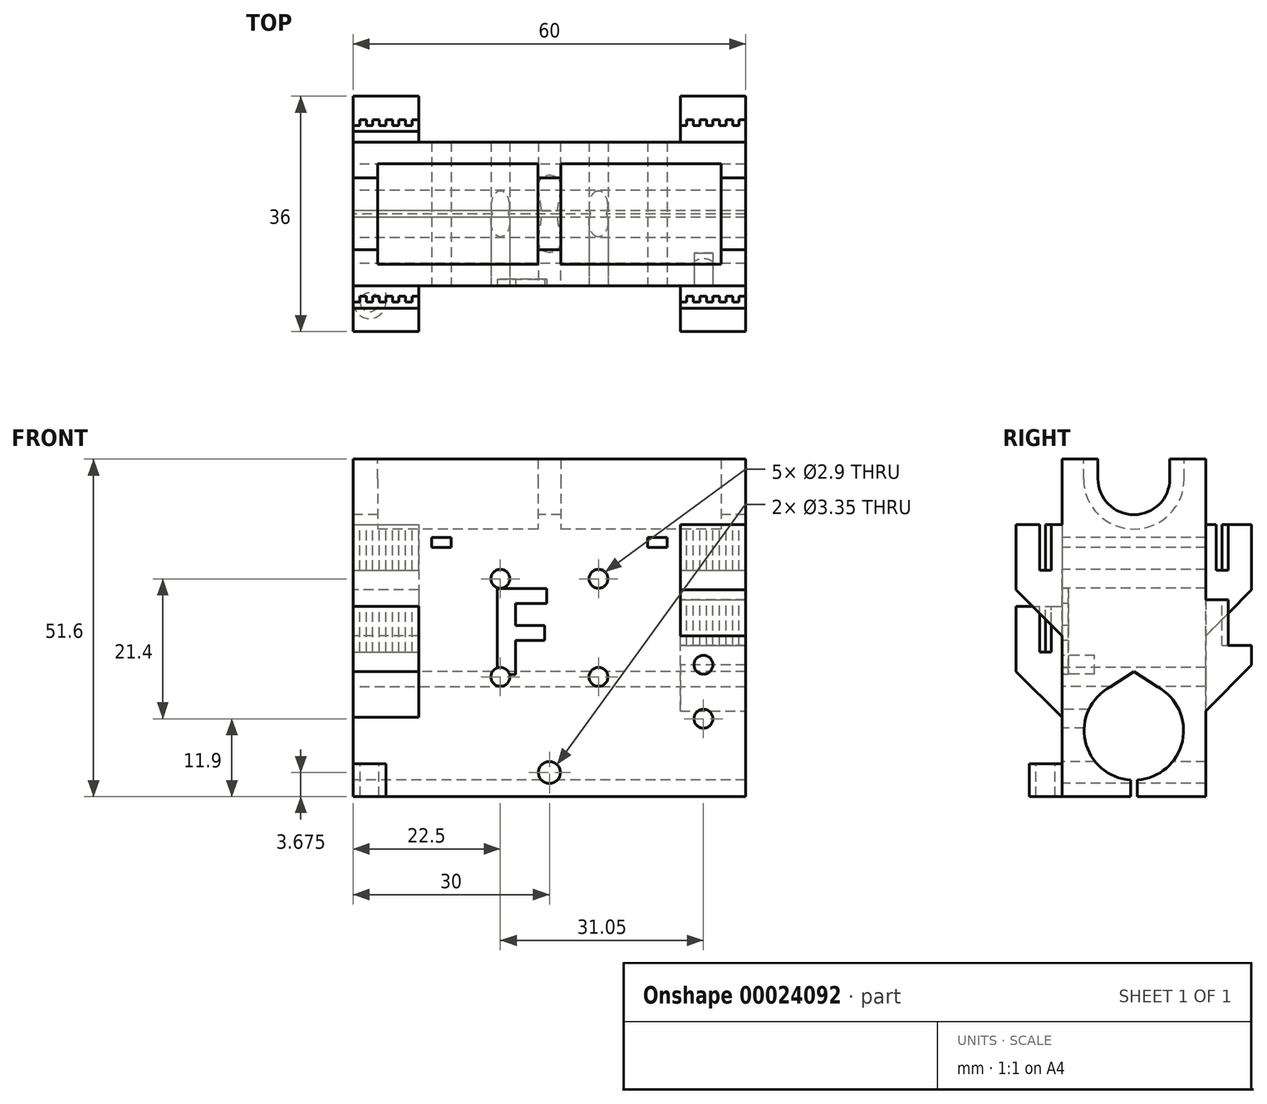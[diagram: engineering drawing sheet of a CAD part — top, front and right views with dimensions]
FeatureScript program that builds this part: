
annotation { "Feature Type Name" : "Feature", "Feature Type Description" : "" }
export const myFeature = defineFeature(function(context is Context, id is Id, definition is map)
    precondition{}
    {
        {
            var Q0;
            Q0=qCreatedBy(makeId("Top.planeOp"),FACE);
            var sketch = newSketch(context, id + "F0", { "sketchPlane" : qUnion([Q0])});
            skLineSegment(sketch, "E0.bottom", {"start": v(0, 0) * mm, "end": v(60, 0) * mm});
            skLineSegment(sketch, "E0.top", {"start": v(0, 22) * mm, "end": v(60, 22) * mm});
            skLineSegment(sketch, "E0.left", {"start": v(0, 0) * mm, "end": v(0, 22) * mm});
            skLineSegment(sketch, "E0.right", {"start": v(60, 0) * mm, "end": v(60, 22) * mm});
            skSolve(sketch);
        }
        {
            var Q0;
            Q0=qSketchRegion(id+"F0",true);
            extrude(context, id + "F1", {"entities" : qUnion([Q0]), "depth" : 51.6 * mm});
        }
        {
            var Q0;
            Q0=makeQuery(id+"F1.opExtrude","SWEPT_FACE",FACE,{"disambiguationData":[OSD([sQuery(id+"F0.wireOp",EDGE,"E0.left")])]});
            var sketch = newSketch(context, id + "F2", { "sketchPlane" : qUnion([Q0])});
            skCircle(sketch, "E1", {"center": v(-11, 10.1) * mm, "radius": 7.6 * mm});
            skCircle(sketch, "E2", {"center": v(-11, 48.6) * mm, "radius": 5.5 * mm});
            skLineSegment(sketch, "E3", {"start": v(-22, 48.6) * mm, "end": v(0, 48.6) * mm, "construction": true});
            skLineSegment(sketch, "E4", {"start": v(-16.5, 51.6) * mm, "end": v(-16.5, 48.6) * mm});
            skLineSegment(sketch, "E5", {"start": v(-5.5, 51.6) * mm, "end": v(-5.5, 48.6) * mm});
            skLineSegment(sketch, "E6", {"start": v(-22, 10.1) * mm, "end": v(0, 10.1) * mm, "construction": true});
            skLineSegment(sketch, "E7", {"start": v(-11, 10.1) * mm, "end": v(-11, 0) * mm, "construction": true});
            skLineSegment(sketch, "E8", {"start": v(-11, 0) * mm, "end": v(-11.5, 0) * mm});
            skLineSegment(sketch, "E9", {"start": v(-11.5, 0) * mm, "end": v(-11.5, 2.52) * mm});
            skLineSegment(sketch, "E10", {"start": v(-11.5, 2.52) * mm, "end": v(-10.5, 2.52) * mm});
            skLineSegment(sketch, "E11", {"start": v(-10.5, 2.52) * mm, "end": v(-10.5, 0) * mm});
            skLineSegment(sketch, "E12", {"start": v(-10.5, 0) * mm, "end": v(-11, 0) * mm});
            skLineSegment(sketch, "E13", {"start": v(-11, 17.7) * mm, "end": v(-11, 19.08) * mm});
            skLineSegment(sketch, "E14", {"start": v(-11, 19.08) * mm, "end": v(-6.5, 16.22) * mm});
            skLineSegment(sketch, "E15", {"start": v(-11, 19.08) * mm, "end": v(-15.5, 16.22) * mm});
            skCircle(sketch, "E16", {"center": v(-11, 48.6) * mm, "radius": 7.7 * mm});
            skLineSegment(sketch, "E17", {"start": v(-3.3, 48.6) * mm, "end": v(-3.3, 51.6) * mm});
            skLineSegment(sketch, "E18", {"start": v(-18.7, 48.6) * mm, "end": v(-18.7, 51.6) * mm});
            skSolve(sketch);
        }
        {
            var Q0;
            {var subQ0=sQuery(id+"F2.wireOp",EDGE,"E14");var subQ1=sQuery(id+"F2.wireOp",EDGE,"E1");var subQ3=makeQuery(id+"F2.imprint","INTERSECT",VERTEX,{"disambiguationData":[OD(0.0)],"derivedFrom":[subQ1,subQ0]});Q0=makeQuery(id+"F2.imprint","IMPRINT",FACE,{"disambiguationData":[TD([[makeQuery(id+"F2.imprint","IMPRINT",EDGE,{"disambiguationData":[TD([[subQ3,-1.0]])],"derivedFrom":subQ1}),1.0]])]});}
            var Q1;
            {var subQ0=sQuery(id+"F2.wireOp",EDGE,"E15");var subQ1=sQuery(id+"F2.wireOp",EDGE,"E1");var subQ3=makeQuery(id+"F2.imprint","INTERSECT",VERTEX,{"disambiguationData":[OD(0.0)],"derivedFrom":[subQ1,subQ0]});Q1=makeQuery(id+"F2.imprint","IMPRINT",FACE,{"disambiguationData":[TD([[makeQuery(id+"F2.imprint","IMPRINT",EDGE,{"disambiguationData":[TD([[subQ3,1.0]])],"derivedFrom":subQ1}),1.0]])]});}
            var Q2;
            Q2=makeQuery(id+"F2.imprint","IMPRINT",FACE,{"disambiguationData":[TD([[makeQuery(id+"F2.imprint","IMPRINT",EDGE,{"derivedFrom":sQuery(id+"F2.wireOp",EDGE,"E8")}),-1.0]])]});
            var Q3;
            {var subQ0=sQuery(id+"F2.wireOp",EDGE,"E10");Q3=makeQuery(id+"F2.imprint","IMPRINT",FACE,{"disambiguationData":[TD([[makeQuery(id+"F2.imprint","IMPRINT",EDGE,{"derivedFrom":subQ0}),-1.0]])]});}
            var Q4;
            {var subQ3=sQuery(id+"F2.wireOp",EDGE,"E13");Q4=makeQuery(id+"F2.imprint","IMPRINT",FACE,{"disambiguationData":[TD([[makeQuery(id+"F2.imprint","IMPRINT",EDGE,{"derivedFrom":subQ3}),-1.0]])]});}
            var Q5;
            {var subQ3=sQuery(id+"F2.wireOp",EDGE,"E13");Q5=makeQuery(id+"F2.imprint","IMPRINT",FACE,{"disambiguationData":[TD([[makeQuery(id+"F2.imprint","IMPRINT",EDGE,{"derivedFrom":subQ3}),1.0]])]});}
            var Q6;
            {var subQ7=sQuery(id+"F2.wireOp",EDGE,"E10");Q6=makeQuery(id+"F2.imprint","IMPRINT",FACE,{"disambiguationData":[TD([[makeQuery(id+"F2.imprint","IMPRINT",EDGE,{"derivedFrom":subQ7}),1.0]])]});}
            var Q7;
            {var subQ3=sQuery(id+"F2.wireOp",EDGE,"E5");Q7=makeQuery(id+"F2.imprint","IMPRINT",FACE,{"disambiguationData":[TD([[makeQuery(id+"F2.imprint","IMPRINT",EDGE,{"derivedFrom":subQ3}),-1.0]])]});}
            var Q8;
            {var subQ0=sQuery(id+"F2.wireOp",EDGE,"E4");Q8=makeQuery(id+"F2.imprint","IMPRINT",FACE,{"disambiguationData":[TD([[makeQuery(id+"F2.imprint","IMPRINT",EDGE,{"derivedFrom":subQ0}),1.0]])]});}
            var Q9;
            {var subQ0=sQuery(id+"F2.wireOp",EDGE,"E4");Q9=makeQuery(id+"F2.imprint","IMPRINT",FACE,{"disambiguationData":[TD([[makeQuery(id+"F2.imprint","IMPRINT",EDGE,{"derivedFrom":subQ0}),1.0]])]});}
            var Q10;
            {var subQ3=sQuery(id+"F2.wireOp",EDGE,"E5");Q10=makeQuery(id+"F2.imprint","IMPRINT",FACE,{"disambiguationData":[TD([[makeQuery(id+"F2.imprint","IMPRINT",EDGE,{"derivedFrom":subQ3}),-1.0]])]});}
            var Q11;
            {var subQ1=sQuery(id+"F2.wireOp",EDGE,"E2");var subQ4=makeQuery(id+"F2.imprint","INTERSECT",VERTEX,{"derivedFrom":[subQ1,sQuery(id+"F2.wireOp",EDGE,"E5")]});Q11=makeQuery(id+"F2.imprint","IMPRINT",FACE,{"disambiguationData":[TD([[makeQuery(id+"F2.imprint","IMPRINT",EDGE,{"disambiguationData":[TD([[subQ4,-1.0]])],"derivedFrom":subQ1}),1.0]])]});}
            extrude(context, id + "F3", {"entities" : qUnion([Q0, Q1, Q2, Q3, Q4, Q5, Q6, Q7, Q8, Q9, Q10, Q11]), "operationType" : NewBodyOperationType.REMOVE, "endBound" : BoundingType.THROUGH_ALL, "oppositeDirection" : true, "depth" : 25 * mm});
        }
        {
            var Q0;
            {var subQ3=sQuery(id+"F2.wireOp",EDGE,"E4");Q0=makeQuery(id+"F2.imprint","IMPRINT",FACE,{"disambiguationData":[TD([[makeQuery(id+"F2.imprint","IMPRINT",EDGE,{"derivedFrom":subQ3}),-1.0]])]});}
            var Q1;
            {var subQ3=sQuery(id+"F2.wireOp",EDGE,"E18");Q1=makeQuery(id+"F2.imprint","IMPRINT",FACE,{"disambiguationData":[TD([[makeQuery(id+"F2.imprint","IMPRINT",EDGE,{"derivedFrom":subQ3}),-1.0]])]});}
            var Q2;
            {var subQ3=sQuery(id+"F2.wireOp",EDGE,"E17");Q2=makeQuery(id+"F2.imprint","IMPRINT",FACE,{"disambiguationData":[TD([[makeQuery(id+"F2.imprint","IMPRINT",EDGE,{"derivedFrom":subQ3}),1.0]])]});}
            extrude(context, id + "F4", {"entities" : qUnion([Q0, Q1, Q2]), "operationType" : NewBodyOperationType.REMOVE, "oppositeDirection" : true, "depth" : 56.25 * mm});
        }
        {
            var Q0;
            {var subQ3=sQuery(id+"F2.wireOp",EDGE,"E4");Q0=makeQuery(id+"F2.imprint","IMPRINT",FACE,{"disambiguationData":[TD([[makeQuery(id+"F2.imprint","IMPRINT",EDGE,{"derivedFrom":subQ3}),-1.0]])]});}
            var Q1;
            {var subQ3=sQuery(id+"F2.wireOp",EDGE,"E18");Q1=makeQuery(id+"F2.imprint","IMPRINT",FACE,{"disambiguationData":[TD([[makeQuery(id+"F2.imprint","IMPRINT",EDGE,{"derivedFrom":subQ3}),-1.0]])]});}
            var Q2;
            {var subQ3=sQuery(id+"F2.wireOp",EDGE,"E17");Q2=makeQuery(id+"F2.imprint","IMPRINT",FACE,{"disambiguationData":[TD([[makeQuery(id+"F2.imprint","IMPRINT",EDGE,{"derivedFrom":subQ3}),1.0]])]});}
            extrude(context, id + "F5", {"entities" : qUnion([Q0, Q1, Q2]), "operationType" : NewBodyOperationType.ADD, "oppositeDirection" : true, "depth" : 31.75 * mm});
        }
        {
            var Q0;
            {var subQ3=sQuery(id+"F2.wireOp",EDGE,"E4");Q0=makeQuery(id+"F2.imprint","IMPRINT",FACE,{"disambiguationData":[TD([[makeQuery(id+"F2.imprint","IMPRINT",EDGE,{"derivedFrom":subQ3}),-1.0]])]});}
            var Q1;
            {var subQ3=sQuery(id+"F2.wireOp",EDGE,"E18");Q1=makeQuery(id+"F2.imprint","IMPRINT",FACE,{"disambiguationData":[TD([[makeQuery(id+"F2.imprint","IMPRINT",EDGE,{"derivedFrom":subQ3}),-1.0]])]});}
            var Q2;
            {var subQ3=sQuery(id+"F2.wireOp",EDGE,"E17");Q2=makeQuery(id+"F2.imprint","IMPRINT",FACE,{"disambiguationData":[TD([[makeQuery(id+"F2.imprint","IMPRINT",EDGE,{"derivedFrom":subQ3}),1.0]])]});}
            extrude(context, id + "F6", {"entities" : qUnion([Q0, Q1, Q2]), "operationType" : NewBodyOperationType.REMOVE, "oppositeDirection" : true, "depth" : 28.25 * mm});
        }
        {
            var Q0;
            {var subQ3=sQuery(id+"F2.wireOp",EDGE,"E4");Q0=makeQuery(id+"F2.imprint","IMPRINT",FACE,{"disambiguationData":[TD([[makeQuery(id+"F2.imprint","IMPRINT",EDGE,{"derivedFrom":subQ3}),-1.0]])]});}
            var Q1;
            {var subQ3=sQuery(id+"F2.wireOp",EDGE,"E18");Q1=makeQuery(id+"F2.imprint","IMPRINT",FACE,{"disambiguationData":[TD([[makeQuery(id+"F2.imprint","IMPRINT",EDGE,{"derivedFrom":subQ3}),-1.0]])]});}
            var Q2;
            {var subQ3=sQuery(id+"F2.wireOp",EDGE,"E17");Q2=makeQuery(id+"F2.imprint","IMPRINT",FACE,{"disambiguationData":[TD([[makeQuery(id+"F2.imprint","IMPRINT",EDGE,{"derivedFrom":subQ3}),1.0]])]});}
            extrude(context, id + "F7", {"entities" : qUnion([Q0, Q1, Q2]), "operationType" : NewBodyOperationType.ADD, "oppositeDirection" : true, "depth" : 3.75 * mm});
        }
        {
            var Q0;
            Q0=makeQuery(id+"F1.opExtrude","SWEPT_FACE",FACE,{"disambiguationData":[OSD([sQuery(id+"F0.wireOp",EDGE,"E0.bottom")])]});
            var sketch = newSketch(context, id + "F8", { "sketchPlane" : qUnion([Q0])});
            skLineSegment(sketch, "E19.bottom", {"start": v(0, 29.1) * mm, "end": v(10, 29.1) * mm});
            skLineSegment(sketch, "E19.top", {"start": v(0, 9.1) * mm, "end": v(10, 9.1) * mm});
            skLineSegment(sketch, "E19.left", {"start": v(0, 29.1) * mm, "end": v(0, 9.1) * mm});
            skLineSegment(sketch, "E19.right", {"start": v(10, 29.1) * mm, "end": v(10, 9.1) * mm});
            skLineSegment(sketch, "E20.bottom", {"start": v(60, 41.6) * mm, "end": v(50, 41.6) * mm});
            skLineSegment(sketch, "E20.top", {"start": v(60, 21.6) * mm, "end": v(50, 21.6) * mm});
            skLineSegment(sketch, "E20.left", {"start": v(60, 41.6) * mm, "end": v(60, 21.6) * mm});
            skLineSegment(sketch, "E20.right", {"start": v(50, 41.6) * mm, "end": v(50, 21.6) * mm});
            skPoint(sketch, "E21", {"position": v(0, 48.6) * mm});
            skPoint(sketch, "E22", {"position": v(0, 8.6) * mm});
            skSolve(sketch);
        }
        {
            var Q0;
            Q0=qSketchRegion(id+"F8",true);
            extrude(context, id + "F9", {"entities" : qUnion([Q0]), "operationType" : NewBodyOperationType.ADD, "depth" : 7 * mm});
        }
        {
            var Q0;
            Q0=makeQuery(id+"F9.opExtrude","CAP_EDGE",EDGE,{"disambiguationData":[OSD([sQuery(id+"F8.wireOp",EDGE,"E19.top")])],"isStart":false});
            var Q1;
            Q1=makeQuery(id+"F9.opExtrude","CAP_EDGE",EDGE,{"disambiguationData":[OSD([sQuery(id+"F8.wireOp",EDGE,"E20.top")])],"isStart":false});
            chamfer(context, id + "F10", {"entities" : qUnion([Q0, Q1]), "width" : 10 * mm, "tangentPropagation" : true});
        }
        {
            var Q0;
            Q0=makeQuery(id+"F9.opExtrude","SWEPT_FACE",FACE,{"disambiguationData":[OSD([sQuery(id+"F8.wireOp",EDGE,"E19.bottom")])]});
            var sketch = newSketch(context, id + "F11", { "sketchPlane" : qUnion([Q0])});
            skLineSegment(sketch, "E23", {"start": v(-935.9, 0) * mm, "end": v(-935.88, -4.54) * mm});
            skLineSegment(sketch, "E24.left", {"start": v(0, -3.4) * mm, "end": v(0, -1.6) * mm});
            skLineSegment(sketch, "E25", {"start": v(6, -2.5) * mm, "end": v(7, -2.5) * mm});
            skLineSegment(sketch, "E26", {"start": v(4, -2.5) * mm, "end": v(5, -2.5) * mm});
            skLineSegment(sketch, "E27", {"start": v(0, -2.5) * mm, "end": v(1, -2.5) * mm});
            skLineSegment(sketch, "E28", {"start": v(7, -1.6) * mm, "end": v(8, -1.6) * mm});
            skLineSegment(sketch, "E29", {"start": v(2, -2.5) * mm, "end": v(3, -2.5) * mm});
            skLineSegment(sketch, "E30", {"start": v(3, -1.6) * mm, "end": v(4, -1.6) * mm});
            skLineSegment(sketch, "E31", {"start": v(8, -2.5) * mm, "end": v(9, -2.5) * mm});
            skLineSegment(sketch, "E32", {"start": v(8, -1.6) * mm, "end": v(8, -2.5) * mm});
            skLineSegment(sketch, "E33", {"start": v(9, -2.5) * mm, "end": v(9, -1.6) * mm});
            skLineSegment(sketch, "E34", {"start": v(10, -1.6) * mm, "end": v(10, -2.5) * mm});
            skLineSegment(sketch, "E35", {"start": v(6, -1.6) * mm, "end": v(6, -2.5) * mm});
            skLineSegment(sketch, "E36", {"start": v(2, -1.6) * mm, "end": v(2, -2.5) * mm});
            skLineSegment(sketch, "E37", {"start": v(1, -1.6) * mm, "end": v(2, -1.6) * mm});
            skLineSegment(sketch, "E38", {"start": v(1, -2.5) * mm, "end": v(1, -1.6) * mm});
            skLineSegment(sketch, "E39", {"start": v(9, -1.6) * mm, "end": v(10, -1.6) * mm});
            skLineSegment(sketch, "E40", {"start": v(5, -1.6) * mm, "end": v(6, -1.6) * mm});
            skLineSegment(sketch, "E41", {"start": v(5, -2.5) * mm, "end": v(5, -1.6) * mm});
            skLineSegment(sketch, "E42", {"start": v(3, -2.5) * mm, "end": v(3, -1.6) * mm});
            skLineSegment(sketch, "E43", {"start": v(4, -1.6) * mm, "end": v(4, -2.5) * mm});
            skLineSegment(sketch, "E44", {"start": v(7, -2.5) * mm, "end": v(7, -1.6) * mm});
            skLineSegment(sketch, "E45", {"start": v(0, -1.6) * mm, "end": v(0, -2.5) * mm});
            skLineSegment(sketch, "E46", {"start": v(10, -2.5) * mm, "end": v(10, -3.4) * mm});
            skLineSegment(sketch, "E47", {"start": v(0, -3.4) * mm, "end": v(10, -3.4) * mm});
            skLineSegment(sketch, "E48", {"start": v(5.3, -1.6) * mm, "end": v(5.3, 0) * mm});
            skSolve(sketch);
        }
        {
            var Q0;
            Q0=qSketchRegion(id+"F11",true);
            extrude(context, id + "F12", {"entities" : qUnion([Q0]), "operationType" : NewBodyOperationType.REMOVE, "oppositeDirection" : true, "depth" : 7 * mm});
        }
        {
            var Q0;
            Q0=makeQuery(id+"F9.opExtrude","SWEPT_FACE",FACE,{"disambiguationData":[OSD([sQuery(id+"F8.wireOp",EDGE,"E20.bottom")])]});
            var sketch = newSketch(context, id + "F13", { "sketchPlane" : qUnion([Q0])});
            skLineSegment(sketch, "E49.left", {"start": v(50, -3.4) * mm, "end": v(50, -1.6) * mm});
            skLineSegment(sketch, "E50", {"start": v(56, -2.5) * mm, "end": v(57, -2.5) * mm});
            skLineSegment(sketch, "E51", {"start": v(54, -2.5) * mm, "end": v(55, -2.5) * mm});
            skLineSegment(sketch, "E52", {"start": v(50, -2.5) * mm, "end": v(51, -2.5) * mm});
            skLineSegment(sketch, "E53", {"start": v(57, -1.6) * mm, "end": v(58, -1.6) * mm});
            skLineSegment(sketch, "E54", {"start": v(52, -2.5) * mm, "end": v(53, -2.5) * mm});
            skLineSegment(sketch, "E55", {"start": v(53, -1.6) * mm, "end": v(54, -1.6) * mm});
            skLineSegment(sketch, "E56", {"start": v(58, -2.5) * mm, "end": v(59, -2.5) * mm});
            skLineSegment(sketch, "E57", {"start": v(58, -1.6) * mm, "end": v(58, -2.5) * mm});
            skLineSegment(sketch, "E58", {"start": v(59, -2.5) * mm, "end": v(59, -1.6) * mm});
            skLineSegment(sketch, "E59", {"start": v(60, -1.6) * mm, "end": v(60, -2.5) * mm});
            skLineSegment(sketch, "E60", {"start": v(56, -1.6) * mm, "end": v(56, -2.5) * mm});
            skLineSegment(sketch, "E61", {"start": v(52, -1.6) * mm, "end": v(52, -2.5) * mm});
            skLineSegment(sketch, "E62", {"start": v(51, -1.6) * mm, "end": v(52, -1.6) * mm});
            skLineSegment(sketch, "E63", {"start": v(51, -2.5) * mm, "end": v(51, -1.6) * mm});
            skLineSegment(sketch, "E64", {"start": v(59, -1.6) * mm, "end": v(60, -1.6) * mm});
            skLineSegment(sketch, "E65", {"start": v(55, -1.6) * mm, "end": v(56, -1.6) * mm});
            skLineSegment(sketch, "E66", {"start": v(55, -2.5) * mm, "end": v(55, -1.6) * mm});
            skLineSegment(sketch, "E67", {"start": v(53, -2.5) * mm, "end": v(53, -1.6) * mm});
            skLineSegment(sketch, "E68", {"start": v(54, -1.6) * mm, "end": v(54, -2.5) * mm});
            skLineSegment(sketch, "E69", {"start": v(57, -2.5) * mm, "end": v(57, -1.6) * mm});
            skLineSegment(sketch, "E70", {"start": v(50, -1.6) * mm, "end": v(50, -2.5) * mm});
            skLineSegment(sketch, "E71", {"start": v(60, -2.5) * mm, "end": v(60, -3.4) * mm});
            skLineSegment(sketch, "E72", {"start": v(50, -3.4) * mm, "end": v(60, -3.4) * mm});
            skLineSegment(sketch, "E73", {"start": v(55.23, -1.6) * mm, "end": v(55.23, 0) * mm});
            skSolve(sketch);
        }
        {
            var Q0;
            Q0=qSketchRegion(id+"F13",true);
            extrude(context, id + "F14", {"entities" : qUnion([Q0]), "operationType" : NewBodyOperationType.REMOVE, "oppositeDirection" : true, "depth" : 7 * mm});
        }
        {
            var Q0;
            Q0=makeQuery(id+"F1.opExtrude","SWEPT_FACE",FACE,{"disambiguationData":[OSD([sQuery(id+"F0.wireOp",EDGE,"E0.top")])]});
            var sketch = newSketch(context, id + "F15", { "sketchPlane" : qUnion([Q0])});
            skLineSegment(sketch, "E74.bottom", {"start": v(-60, 10.1) * mm, "end": v(-50, 10.1) * mm});
            skLineSegment(sketch, "E74.top", {"start": v(-60, 30.1) * mm, "end": v(-50, 30.1) * mm});
            skLineSegment(sketch, "E74.left", {"start": v(-60, 10.1) * mm, "end": v(-60, 30.1) * mm});
            skLineSegment(sketch, "E74.right", {"start": v(-50, 10.1) * mm, "end": v(-50, 30.1) * mm});
            skLineSegment(sketch, "E75.bottom", {"start": v(0, 41.6) * mm, "end": v(-10, 41.6) * mm});
            skLineSegment(sketch, "E75.top", {"start": v(0, 21.6) * mm, "end": v(-10, 21.6) * mm});
            skLineSegment(sketch, "E75.left", {"start": v(0, 41.6) * mm, "end": v(0, 21.6) * mm});
            skLineSegment(sketch, "E75.right", {"start": v(-10, 41.6) * mm, "end": v(-10, 21.6) * mm});
            skSolve(sketch);
        }
        {
            var Q0;
            Q0=qSketchRegion(id+"F15",true);
            extrude(context, id + "F16", {"entities" : qUnion([Q0]), "operationType" : NewBodyOperationType.ADD, "depth" : 7 * mm});
        }
        {
            var Q0;
            Q0=makeQuery(id+"F16.opExtrude","SWEPT_FACE",FACE,{"disambiguationData":[OSD([sQuery(id+"F15.wireOp",EDGE,"E74.top")])]});
            var sketch = newSketch(context, id + "F17", { "sketchPlane" : qUnion([Q0])});
            skLineSegment(sketch, "E76.left", {"start": v(50, 23.6) * mm, "end": v(50, 25.4) * mm});
            skLineSegment(sketch, "E77", {"start": v(56, 24.5) * mm, "end": v(57, 24.5) * mm});
            skLineSegment(sketch, "E78", {"start": v(54, 24.5) * mm, "end": v(55, 24.5) * mm});
            skLineSegment(sketch, "E79", {"start": v(50, 24.5) * mm, "end": v(51, 24.5) * mm});
            skLineSegment(sketch, "E80", {"start": v(57, 25.4) * mm, "end": v(58, 25.4) * mm});
            skLineSegment(sketch, "E81", {"start": v(52, 24.5) * mm, "end": v(53, 24.5) * mm});
            skLineSegment(sketch, "E82", {"start": v(53, 25.4) * mm, "end": v(54, 25.4) * mm});
            skLineSegment(sketch, "E83", {"start": v(58, 24.5) * mm, "end": v(59, 24.5) * mm});
            skLineSegment(sketch, "E84", {"start": v(58, 25.4) * mm, "end": v(58, 24.5) * mm});
            skLineSegment(sketch, "E85", {"start": v(59, 24.5) * mm, "end": v(59, 25.4) * mm});
            skLineSegment(sketch, "E86", {"start": v(60, 25.4) * mm, "end": v(60, 24.5) * mm});
            skLineSegment(sketch, "E87", {"start": v(56, 25.4) * mm, "end": v(56, 24.5) * mm});
            skLineSegment(sketch, "E88", {"start": v(52, 25.4) * mm, "end": v(52, 24.5) * mm});
            skLineSegment(sketch, "E89", {"start": v(51, 25.4) * mm, "end": v(52, 25.4) * mm});
            skLineSegment(sketch, "E90", {"start": v(51, 24.5) * mm, "end": v(51, 25.4) * mm});
            skLineSegment(sketch, "E91", {"start": v(59, 25.4) * mm, "end": v(60, 25.4) * mm});
            skLineSegment(sketch, "E92", {"start": v(55, 25.4) * mm, "end": v(56, 25.4) * mm});
            skLineSegment(sketch, "E93", {"start": v(55, 24.5) * mm, "end": v(55, 25.4) * mm});
            skLineSegment(sketch, "E94", {"start": v(53, 24.5) * mm, "end": v(53, 25.4) * mm});
            skLineSegment(sketch, "E95", {"start": v(54, 25.4) * mm, "end": v(54, 24.5) * mm});
            skLineSegment(sketch, "E96", {"start": v(57, 24.5) * mm, "end": v(57, 25.4) * mm});
            skLineSegment(sketch, "E97", {"start": v(50, 25.4) * mm, "end": v(50, 24.5) * mm});
            skLineSegment(sketch, "E98", {"start": v(60, 24.5) * mm, "end": v(60, 23.6) * mm});
            skLineSegment(sketch, "E99", {"start": v(50, 23.6) * mm, "end": v(60, 23.6) * mm});
            skLineSegment(sketch, "E100", {"start": v(55, 23.6) * mm, "end": v(55, 22) * mm});
            skSolve(sketch);
        }
        {
            var Q0;
            {var subQ4=sQuery(id+"F17.wireOp",EDGE,"E76.left");Q0=makeQuery(id+"F17.imprint","IMPRINT",FACE,{"disambiguationData":[TD([[makeQuery(id+"F17.imprint","IMPRINT",EDGE,{"derivedFrom":subQ4}),1.0]])]});}
            extrude(context, id + "F18", {"entities" : qUnion([Q0]), "operationType" : NewBodyOperationType.REMOVE, "oppositeDirection" : true, "depth" : 7 * mm});
        }
        {
            var Q0;
            Q0=makeQuery(id+"F16.opExtrude","SWEPT_FACE",FACE,{"disambiguationData":[OSD([sQuery(id+"F15.wireOp",EDGE,"E75.bottom")])]});
            var sketch = newSketch(context, id + "F19", { "sketchPlane" : qUnion([Q0])});
            skLineSegment(sketch, "E101", {"start": v(6, 24.5) * mm, "end": v(7, 24.5) * mm});
            skLineSegment(sketch, "E102", {"start": v(4, 24.5) * mm, "end": v(5, 24.5) * mm});
            skLineSegment(sketch, "E103", {"start": v(0, 24.5) * mm, "end": v(1, 24.5) * mm});
            skLineSegment(sketch, "E104", {"start": v(7, 25.4) * mm, "end": v(8, 25.4) * mm});
            skLineSegment(sketch, "E105", {"start": v(2, 24.5) * mm, "end": v(3, 24.5) * mm});
            skLineSegment(sketch, "E106", {"start": v(3, 25.4) * mm, "end": v(4, 25.4) * mm});
            skLineSegment(sketch, "E107", {"start": v(8, 24.5) * mm, "end": v(9, 24.5) * mm});
            skLineSegment(sketch, "E108", {"start": v(8, 25.4) * mm, "end": v(8, 24.5) * mm});
            skLineSegment(sketch, "E109", {"start": v(9, 24.5) * mm, "end": v(9, 25.4) * mm});
            skLineSegment(sketch, "E110", {"start": v(10, 25.4) * mm, "end": v(10, 24.5) * mm});
            skLineSegment(sketch, "E111", {"start": v(6, 25.4) * mm, "end": v(6, 24.5) * mm});
            skLineSegment(sketch, "E112", {"start": v(2, 25.4) * mm, "end": v(2, 24.5) * mm});
            skLineSegment(sketch, "E113", {"start": v(1, 25.4) * mm, "end": v(2, 25.4) * mm});
            skLineSegment(sketch, "E114", {"start": v(1, 24.5) * mm, "end": v(1, 25.4) * mm});
            skLineSegment(sketch, "E115", {"start": v(9, 25.4) * mm, "end": v(10, 25.4) * mm});
            skLineSegment(sketch, "E116", {"start": v(5, 25.4) * mm, "end": v(6, 25.4) * mm});
            skLineSegment(sketch, "E117", {"start": v(5, 24.5) * mm, "end": v(5, 25.4) * mm});
            skLineSegment(sketch, "E118", {"start": v(3, 24.5) * mm, "end": v(3, 25.4) * mm});
            skLineSegment(sketch, "E119", {"start": v(4, 25.4) * mm, "end": v(4, 24.5) * mm});
            skLineSegment(sketch, "E120", {"start": v(7, 24.5) * mm, "end": v(7, 25.4) * mm});
            skLineSegment(sketch, "E121", {"start": v(10, 24.5) * mm, "end": v(10, 23.6) * mm});
            skLineSegment(sketch, "E122", {"start": v(0, 23.6) * mm, "end": v(10, 23.6) * mm});
            skLineSegment(sketch, "E123", {"start": v(5, 23.6) * mm, "end": v(5, 22) * mm});
            skLineSegment(sketch, "E124", {"start": v(0, 23.6) * mm, "end": v(0, 24.5) * mm});
            skSolve(sketch);
        }
        {
            var Q0;
            Q0=makeQuery(id+"F19.imprint","IMPRINT",FACE,{"disambiguationData":[TD([[makeQuery(id+"F19.imprint","IMPRINT",EDGE,{"derivedFrom":sQuery(id+"F19.wireOp",EDGE,"E101")}),-1.0]])]});
            extrude(context, id + "F20", {"entities" : qUnion([Q0]), "operationType" : NewBodyOperationType.REMOVE, "oppositeDirection" : true, "depth" : 7 * mm});
        }
        {
            var Q0;
            Q0=makeQuery(id+"F16.opExtrude","CAP_EDGE",EDGE,{"disambiguationData":[OSD([sQuery(id+"F15.wireOp",EDGE,"E75.top")])],"isStart":false});
            var Q1;
            Q1=makeQuery(id+"F16.opExtrude","CAP_EDGE",EDGE,{"disambiguationData":[OSD([sQuery(id+"F15.wireOp",EDGE,"E74.bottom")])],"isStart":false});
            chamfer(context, id + "F21", {"entities" : qUnion([Q0, Q1]), "width" : 10 * mm, "tangentPropagation" : true});
        }
        {
            var Q0;
            Q0=makeQuery(id+"F1.opExtrude","SWEPT_FACE",FACE,{"disambiguationData":[OSD([sQuery(id+"F0.wireOp",EDGE,"E0.bottom")])]});
            var sketch = newSketch(context, id + "F22", { "sketchPlane" : qUnion([Q0])});
            skCircle(sketch, "E125", {"center": v(22.5, 33.3) * mm, "radius": 1.45 * mm});
            skCircle(sketch, "E126", {"center": v(37.5, 33.3) * mm, "radius": 1.45 * mm});
            skCircle(sketch, "E127", {"center": v(22.5, 18.3) * mm, "radius": 1.45 * mm});
            skCircle(sketch, "E128", {"center": v(37.5, 18.3) * mm, "radius": 1.45 * mm});
            skLineSegment(sketch, "E129", {"start": v(22.5, 33.3) * mm, "end": v(0, 33.3) * mm});
            skLineSegment(sketch, "E130", {"start": v(37.5, 18.3) * mm, "end": v(60, 18.3) * mm});
            skLineSegment(sketch, "E131", {"start": v(37.5, 33.3) * mm, "end": v(37.5, 51.6) * mm});
            skLineSegment(sketch, "E132", {"start": v(22.5, 18.3) * mm, "end": v(22.5, 0) * mm});
            skCircle(sketch, "E133", {"center": v(30, 3.68) * mm, "radius": 1.68 * mm});
            skLineSegment(sketch, "E134", {"start": v(30, 0) * mm, "end": v(30, 13.82) * mm, "construction": true});
            skSolve(sketch);
        }
        {
            var Q0;
            Q0=qSketchRegion(id+"F22",true);
            var Q1;
            Q1=makeQuery(id+"F22.imprint","IMPRINT",FACE,{"disambiguationData":[TD([[makeQuery(id+"F22.imprint","IMPRINT",EDGE,{"derivedFrom":sQuery(id+"F22.wireOp",EDGE,"E125")}),1.0]])]});
            var Q2;
            Q2=makeQuery(id+"F22.imprint","IMPRINT",FACE,{"disambiguationData":[TD([[makeQuery(id+"F22.imprint","IMPRINT",EDGE,{"derivedFrom":sQuery(id+"F22.wireOp",EDGE,"E126")}),1.0]])]});
            var Q3;
            Q3=makeQuery(id+"F22.imprint","IMPRINT",FACE,{"disambiguationData":[TD([[makeQuery(id+"F22.imprint","IMPRINT",EDGE,{"derivedFrom":sQuery(id+"F22.wireOp",EDGE,"E128")}),1.0]])]});
            var Q4;
            Q4=makeQuery(id+"F22.imprint","IMPRINT",FACE,{"disambiguationData":[TD([[makeQuery(id+"F22.imprint","IMPRINT",EDGE,{"derivedFrom":sQuery(id+"F22.wireOp",EDGE,"E127")}),1.0]])]});
            extrude(context, id + "F23", {"entities" : qUnion([Q0, Q1, Q2, Q3, Q4]), "operationType" : NewBodyOperationType.REMOVE, "endBound" : BoundingType.THROUGH_ALL, "oppositeDirection" : true, "depth" : 25 * mm});
        }
        {
            var Q0;
            Q0=makeQuery(id+"F1.opExtrude","SWEPT_FACE",FACE,{"disambiguationData":[OSD([sQuery(id+"F0.wireOp",EDGE,"E0.bottom")])]});
            var sketch = newSketch(context, id + "F24", { "sketchPlane" : qUnion([Q0])});
            skCircle(sketch, "E135", {"center": v(53.55, 20.15) * mm, "radius": 1.45 * mm});
            skCircle(sketch, "E136", {"center": v(53.55, 11.9) * mm, "radius": 1.45 * mm});
            skSolve(sketch);
        }
        {
            var Q0;
            Q0=qSketchRegion(id+"F24",true);
            extrude(context, id + "F25", {"entities" : qUnion([Q0]), "operationType" : NewBodyOperationType.REMOVE, "oppositeDirection" : true, "depth" : 5 * mm});
        }
        {
            var Q0;
            Q0=makeQuery(id+"F1.opExtrude","SWEPT_FACE",FACE,{"disambiguationData":[OSD([sQuery(id+"F0.wireOp",EDGE,"E0.bottom")])]});
            var sketch = newSketch(context, id + "F26", { "sketchPlane" : qUnion([Q0])});
            skText(sketch, "E137", { "text": "F", "fontName": "OpenSans-Bold.ttf"});
            skLineSegment(sketch, "E138", {"start": v(22.5, 33.3) * mm, "end": v(22.5, 18.3) * mm, "construction": true});
            skLineSegment(sketch, "E139", {"start": v(22.5, 18.3) * mm, "end": v(37.5, 18.3) * mm, "construction": true});
            skLineSegment(sketch, "E140", {"start": v(37.5, 18.3) * mm, "end": v(37.5, 33.3) * mm, "construction": true});
            skLineSegment(sketch, "E141", {"start": v(37.5, 33.3) * mm, "end": v(22.5, 33.3) * mm, "construction": true});
            skLineSegment(sketch, "E142", {"start": v(22.5, 25.8) * mm, "end": v(25.4, 25.8) * mm, "construction": true});
            skLineSegment(sketch, "E143", {"start": v(34.6, 25.8) * mm, "end": v(37.5, 25.8) * mm, "construction": true});
            skLineSegment(sketch, "E144", {"start": v(30, 19.16) * mm, "end": v(30, 18.3) * mm, "construction": true});
            skLineSegment(sketch, "E145", {"start": v(30, 33.3) * mm, "end": v(30, 32.44) * mm, "construction": true});
            const initialGuessF26  = {"E137": [0.0204, 0.01866, 1, 0, 0.01328]};
            skSetInitialGuess(sketch, initialGuessF26);
            skSolve(sketch);
        }
        {
            var Q0;
            Q0=qSketchRegion(id+"F26",true);
            extrude(context, id + "F27", {"entities" : qUnion([Q0]), "operationType" : NewBodyOperationType.REMOVE, "oppositeDirection" : true, "depth" : 1 * mm});
        }
        {
            var Q0;
            Q0=makeQuery(id+"F1.opExtrude","SWEPT_FACE",FACE,{"disambiguationData":[OSD([sQuery(id+"F0.wireOp",EDGE,"E0.bottom")])]});
            var sketch = newSketch(context, id + "F28", { "sketchPlane" : qUnion([Q0])});
            skLineSegment(sketch, "E146.bottom", {"start": v(0, 0) * mm, "end": v(5, 0) * mm});
            skLineSegment(sketch, "E146.top", {"start": v(0, 5) * mm, "end": v(5, 5) * mm});
            skLineSegment(sketch, "E146.left", {"start": v(0, 0) * mm, "end": v(0, 5) * mm});
            skLineSegment(sketch, "E146.right", {"start": v(5, 0) * mm, "end": v(5, 5) * mm});
            skSolve(sketch);
        }
        {
            var Q0;
            Q0=qSketchRegion(id+"F28",true);
            extrude(context, id + "F29", {"entities" : qUnion([Q0]), "operationType" : NewBodyOperationType.ADD, "depth" : 5 * mm});
        }
        {
            var Q0;
            Q0=makeQuery(id+"F29.opExtrude","SWEPT_FACE",FACE,{"disambiguationData":[OSD([sQuery(id+"F28.wireOp",EDGE,"E146.top")])]});
            var sketch = newSketch(context, id + "F30", { "sketchPlane" : qUnion([Q0])});
            skCircle(sketch, "E147", {"center": v(2.5, -2.5) * mm, "radius": 1.45 * mm});
            skLineSegment(sketch, "E148", {"start": v(0, -2.5) * mm, "end": v(5, -2.5) * mm});
            skSolve(sketch);
        }
        {
            var Q0;
            Q0=qSketchRegion(id+"F30",true);
            extrude(context, id + "F31", {"entities" : qUnion([Q0]), "operationType" : NewBodyOperationType.REMOVE, "oppositeDirection" : true, "depth" : 25 * mm});
        }
        {
            var Q0;
            Q0=makeQuery(id+"F29.opExtrude","CAP_EDGE",EDGE,{"disambiguationData":[OSD([sQuery(id+"F28.wireOp",EDGE,"E146.left")])],"isStart":false});
            var Q1;
            Q1=makeQuery(id+"F29.opExtrude","CAP_EDGE",EDGE,{"disambiguationData":[OSD([sQuery(id+"F28.wireOp",EDGE,"E146.right")])],"isStart":false});
            fillet(context, id + "F32", {"entities" : qUnion([Q0, Q1]), "radius" : 2.5 * mm, "tangentPropagation" : true, "allowEdgeOverflow" : false});
        }
        {
            var Q0;
            Q0=makeQuery(id+"F1.opExtrude","SWEPT_FACE",FACE,{"disambiguationData":[OSD([sQuery(id+"F0.wireOp",EDGE,"E0.bottom")])]});
            var sketch = newSketch(context, id + "F33", { "sketchPlane" : qUnion([Q0])});
            skLineSegment(sketch, "E149.bottom", {"start": v(12, 39.6) * mm, "end": v(15, 39.6) * mm});
            skLineSegment(sketch, "E149.top", {"start": v(12, 38.1) * mm, "end": v(15, 38.1) * mm});
            skLineSegment(sketch, "E149.left", {"start": v(12, 39.6) * mm, "end": v(12, 38.1) * mm});
            skLineSegment(sketch, "E149.right", {"start": v(15, 39.6) * mm, "end": v(15, 38.1) * mm});
            skLineSegment(sketch, "E150", {"start": v(30, 51.6) * mm, "end": v(30, 35.77) * mm, "construction": true});
            skLineSegment(sketch, "E151.MirrorCS", {"start": v(48, 39.6) * mm, "end": v(48, 38.1) * mm});
            skLineSegment(sketch, "E152.MirrorCS", {"start": v(45, 39.6) * mm, "end": v(45, 38.1) * mm});
            skLineSegment(sketch, "E153.MirrorCS", {"start": v(48, 39.6) * mm, "end": v(45, 39.6) * mm});
            skLineSegment(sketch, "E154.MirrorCS", {"start": v(48, 38.1) * mm, "end": v(45, 38.1) * mm});
            skSolve(sketch);
        }
        {
            var Q0;
            Q0=makeQuery(id+"F33.imprint","IMPRINT",FACE,{"disambiguationData":[TD([[makeQuery(id+"F33.imprint","IMPRINT",EDGE,{"derivedFrom":sQuery(id+"F33.wireOp",EDGE,"E149.bottom")}),-1.0]])]});
            var Q1;
            Q1=makeQuery(id+"F33.imprint","IMPRINT",FACE,{"disambiguationData":[TD([[makeQuery(id+"F33.imprint","IMPRINT",EDGE,{"derivedFrom":sQuery(id+"F33.wireOp",EDGE,"E151.MirrorCS")}),-1.0]])]});
            extrude(context, id + "F34", {"entities" : qUnion([Q0, Q1]), "operationType" : NewBodyOperationType.REMOVE, "endBound" : BoundingType.THROUGH_ALL, "oppositeDirection" : true, "depth" : 25 * mm});
        }
    });
